# Revit family: Deca_Misturador monocomando de mesa para cozinha_Colore_2289
name_source: partatom
category: Plumbing Fixtures
units: mm (PartAtom-declared; Revit-internal decimal feet)

## family parameters
Cut with Voids When Loaded = No
Host = Face
Part Type = Normal
Room Calculation Point = No
Round Connector Dimension = Use Radius
Shared = No

## types (20) — shared parameters
Acompanha o Produto = Acompanha Ligação Flexivel
Aprovado por = quattroD
Atendimento ao Cliente = 0800-0117073
Categoria = METAIS PARA COZINHA
Composição Anel Vedação = -
Composição Assento = -
Composição Básica = Liga de Cobre (bronze e latão),Plásticos de Engenharia,Elastômeros
Composição Componente = -
Consumo = -
Cor Interna = -
Cores Componente = -
Criado por = quattroD
Código Pai = 2289
Description = Misturador monocomando de mesa para cozinha
Diâmetro Água Fria = 15 mm  [stored 0.0492126 ft]
Diâmetro Água Quente = 15 mm  [stored 0.0492126 ft]
Informações Complementares = -
Itens de Instalação = -
Linha = Colore
Manufacturer = Deca
Norma = Não Possui
Pressão máx. funcionamento = 40 MCA
Pressão mín. Aquec. Acúmulo = 10 MCA
Pressão mín. Aquec. Passagem = 18 MCA
Pressão mín. funcionamento = 10 MCA
Raio Água Fria = 8 mm  [stored 0.0262467 ft]
Raio Água Quente = 8 mm  [stored 0.0262467 ft]
Saída de Esgoto = -
Segmento = Banheiro Luxo
Tipo de dispositivo economizador = Não
Tipo de mecanismo utilizado = Cartucho Monocomando
Tipo de rosca de entrada = BSP NBR 8133
Tipo de rosca de saída = -
URL = www.deca.com.br
Vazão na Pressão máx. (L/min) = 15
Vazão na Pressão mín. (L/min) = 4
zero-valued in all types: Default Elevation

## per-type parameters (varying)
| type | Cor Principal | Cor Secundária | Material | Material Secundário | Model | Peso Líquido (Kg) |
| 2289.C.PT_Cromado - Preto | Cromado | Preto | Deca_Cromado | Deca_Preto | 2289.C.PT | 3.191 |
| 2289.CT.MT.PT_Corten - Preto | Corten | Preto | Deca_Corten | Deca_Preto | 2289.CT.MT.PT | 3.314 |
| 2289.CT.MT.FD_Corten - Fendi | Corten | Fendi | Deca_Corten | Deca_Fendi | 2289.CT.MT.FD | 3.34 |
| 2289.CT.MT.TC_Corten - Terracota | Corten | Terracota | Deca_Corten | Deca_Terracota | 2289.CT.MT.TC | 3.44 |
| 2289.C.TC_Cromado - Terracota | Cromado | Terracota | Deca_Cromado | Deca_Terracota | 2289.C.TC | 3.191 |
| 2289.INX.TC_Inox - Terracota | Inox | Terracota | Deca_Inox | Deca_Terracota | 2289.INX.TC | 3.466 |
| 2289.BL.MT.FD_Black Matte - Fendi | Black Matte | Fendi | Deca_Black Matte | Deca_Fendi | 2289.BL.MT.FD | 3.466 |
| 2289.GL.RD.FD_Red Gold - Fendi | Red Gold | Fendi | Deca_Red Gold | Deca_Fendi | 2289.GL.RD.FD | 3.191 |
| 2289.C.FD_Cromado - Fendi | Cromado | Fendi | Deca_Cromado | Deca_Fendi | 2289.C.FD | 3.466 |
| 2289.GL.RD.MR_Red Gold - Marrom | Red Gold | Marrom | Deca_Red Gold | Deca_Marrom | 2289.GL.RD.MR | 3.217 |
| 2289.C.MR_Cromado - Marrom | Cromado | Marrom | Deca_Cromado | Deca_Marrom | 2289.C.MR | 3.44 |
| 2289.INX.FD_Inox - Fendi | Inox | Fendi | Deca_Inox | Deca_Fendi | 2289.INX.FD | 3.44 |
| 2289.BL.MT.TC_Black Matte - Terracota | Black Matte | Terracota | Deca_Black Matte | Deca_Terracota | 2289.BL.MT.TC | 3.44 |
| 2289.CT.MT.MR_Corten - Marrom | Corten | Marrom | Deca_Corten | Deca_Marrom | 2289.CT.MT.MR | 3.34 |
| 2289.GL.RD.TC_Red Gold - Terracota | Red Gold | Terracota | Deca_Red Gold | Deca_Terracota | 2289.GL.RD.TC | 3.44 |
| 2289.BL.MT.MR_Black Matte - Marrom | Black Matte | Marrom | Deca_Black Matte | Deca_Marrom | 2289.BL.MT.MR | 3.34 |
| 2289.GL.RD.PT_Red Gold - Preto | Red Gold | Preto | Deca_Red Gold | Deca_Preto | 2289.GL.RD.PT | 3.217 |
| 2289.INX.PT_Inox - Preto | Inox | Preto | Deca_Inox | Deca_Preto | 2289.INX.PT | 3.44 |
| 2289.BL.MT.PT_Black Matte - Preto | Black Matte | Preto | Deca_Black Matte | Deca_Preto | 2289.BL.MT.PT | 3.34 |
| 2289.INX.MR_Inox - Marrom | Inox | Marrom | Deca_Inox | Deca_Marrom | 2289.INX.MR | 3.44 |

note: source unit labels omitted for Vazão na Pressão máx. (L/min), Vazão na Pressão mín. (L/min) — the stored unit's dimension contradicts the parameter name (converter mislabeling)

note: [stored X ft] marks values corroborated as IEEE doubles in the binary element streams (Revit-internal decimal feet)

## geometry (parser evidence)
native form markers: Sweep x2
no freeform markers — native parametric forms only
